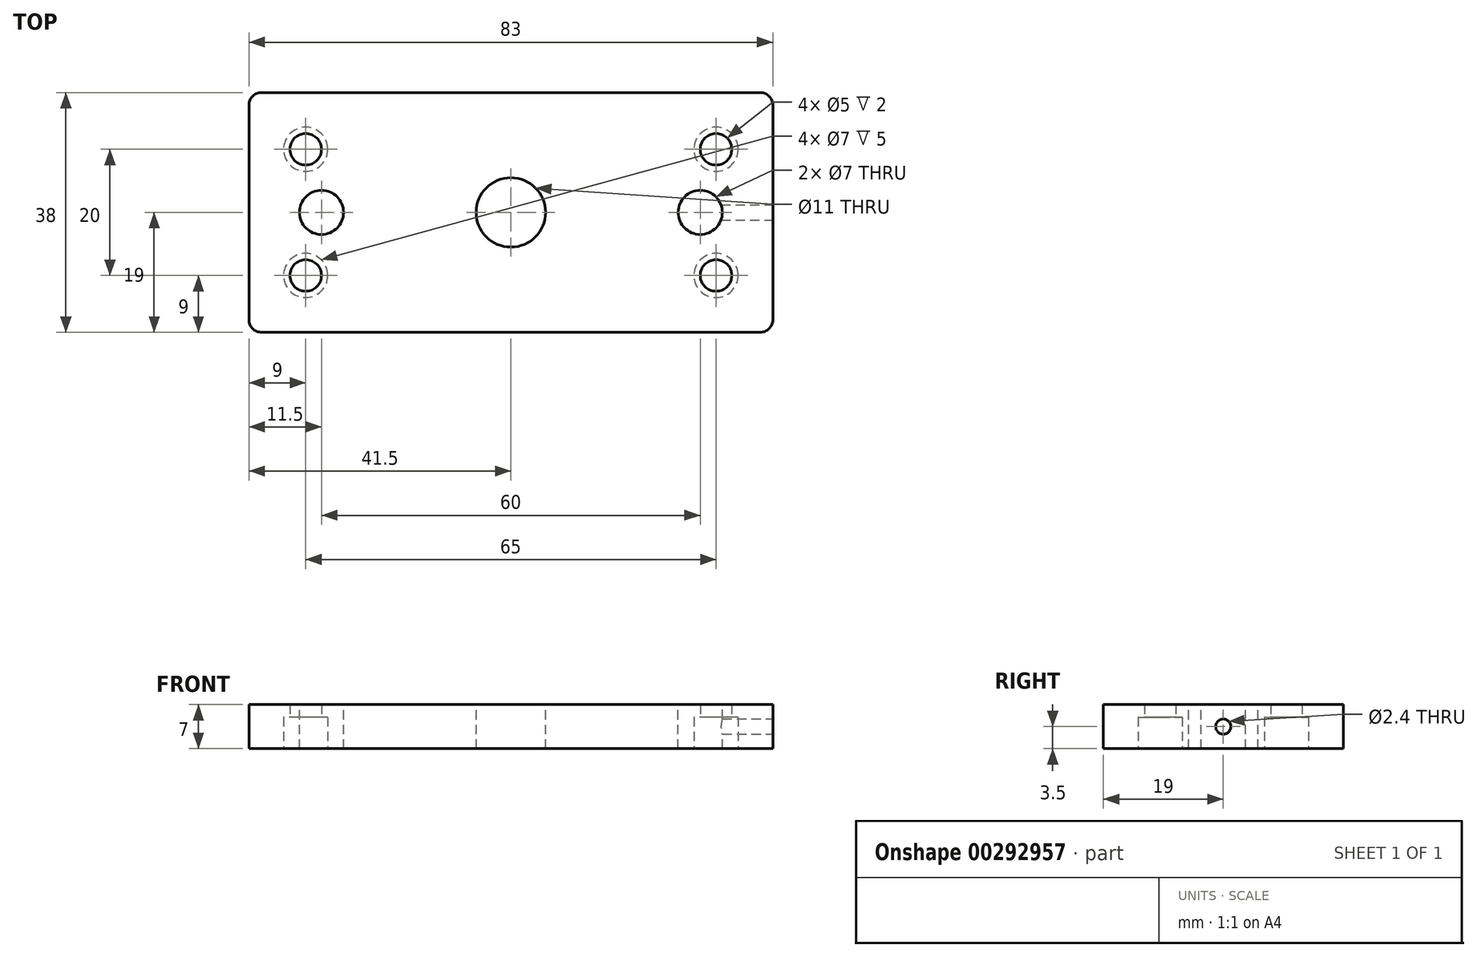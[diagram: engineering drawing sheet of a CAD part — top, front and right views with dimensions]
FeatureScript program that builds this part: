
annotation { "Feature Type Name" : "Feature", "Feature Type Description" : "" }
export const myFeature = defineFeature(function(context is Context, id is Id, definition is map)
    precondition{}
    {
        {
            var Q0;
            Q0=qCreatedBy(makeId("Top.planeOp"),FACE);
            var sketch = newSketch(context, id + "F0", { "sketchPlane" : qUnion([Q0])});
            skLineSegment(sketch, "E0.bottom", {"start": v(0, 0) * mm, "end": v(-65, 0) * mm});
            skLineSegment(sketch, "E0.top", {"start": v(0, 20) * mm, "end": v(-65, 20) * mm});
            skLineSegment(sketch, "E0.left", {"start": v(0, 0) * mm, "end": v(0, 20) * mm});
            skLineSegment(sketch, "E0.right", {"start": v(-65, 0) * mm, "end": v(-65, 20) * mm});
            skLineSegment(sketch, "E1.0", {"start": v(7, 29) * mm, "end": v(-72, 29) * mm});
            skLineSegment(sketch, "E1.1", {"start": v(9, -7) * mm, "end": v(9, 27) * mm});
            skLineSegment(sketch, "E1.2", {"start": v(7, -9) * mm, "end": v(-72, -9) * mm});
            skLineSegment(sketch, "E1.3", {"start": v(-74, -7) * mm, "end": v(-74, 27) * mm});
            skPoint(sketch, "E2.visualSharp", {"position": v(-74, 29) * mm});
            skArc(sketch, "E2.filletArc", {"start": v(-72, 29) * mm, "mid": v(-73.41, 28.41) * mm, "end": v(-74, 27) * mm});
            skPoint(sketch, "E3.visualSharp", {"position": v(-74, -9) * mm});
            skArc(sketch, "E3.filletArc", {"start": v(-74, -7) * mm, "mid": v(-73.41, -8.41) * mm, "end": v(-72, -9) * mm});
            skPoint(sketch, "E4.visualSharp", {"position": v(9, -9) * mm});
            skArc(sketch, "E4.filletArc", {"start": v(7, -9) * mm, "mid": v(8.41, -8.41) * mm, "end": v(9, -7) * mm});
            skPoint(sketch, "E5.visualSharp", {"position": v(9, 29) * mm});
            skArc(sketch, "E5.filletArc", {"start": v(9, 27) * mm, "mid": v(8.41, 28.41) * mm, "end": v(7, 29) * mm});
            skSolve(sketch);
        }
        {
            var Q0;
            Q0=makeQuery(id+"F0.imprint","IMPRINT",FACE,{"disambiguationData":[TD([[makeQuery(id+"F0.imprint","IMPRINT",EDGE,{"derivedFrom":sQuery(id+"F0.wireOp",EDGE,"E0.bottom")}),1.0]])]});
            var Q1;
            Q1=makeQuery(id+"F0.imprint","IMPRINT",FACE,{"disambiguationData":[TD([[makeQuery(id+"F0.imprint","IMPRINT",EDGE,{"derivedFrom":sQuery(id+"F0.wireOp",EDGE,"E0.bottom")}),-1.0]])]});
            extrude(context, id + "F1", {"entities" : qUnion([Q0, Q1]), "depth" : 7 * mm});
        }
        {
            var Q0;
            Q0=sQuery(id+"F0.wireOp",VERTEX,"E0.right.end");
            var Q1;
            Q1=sQuery(id+"F0.wireOp",VERTEX,"E0.right.start");
            var Q2;
            Q2=sQuery(id+"F0.wireOp",VERTEX,"E0.left.start");
            var Q3;
            Q3=sQuery(id+"F0.wireOp",VERTEX,"E0.left.end");
            var Q4;
            Q4=makeQuery(id+"F1.opExtrude","SWEPT_BODY",BODY,{"disambiguationData":[OSD([sQuery(id+"F0.wireOp",EDGE,"E1.0"),sQuery(id+"F0.wireOp",EDGE,"E1.1"),sQuery(id+"F0.wireOp",EDGE,"E1.2"),sQuery(id+"F0.wireOp",EDGE,"E1.3"),sQuery(id+"F0.wireOp",EDGE,"E2.filletArc"),sQuery(id+"F0.wireOp",EDGE,"E3.filletArc"),sQuery(id+"F0.wireOp",EDGE,"E4.filletArc"),sQuery(id+"F0.wireOp",EDGE,"E5.filletArc")])]});
            hole(context, id + "F2", {"style" : HoleStyle.SIMPLE, "endStyle" : HoleEndStyle.THROUGH, "oppositeDirection" : true, "holeDiameter" : 5 * mm, "tappedDepth" : 12 * mm, "tapClearance" : 3, "locations" : qUnion([Q0, Q1, Q2, Q3]), "scope" : qUnion([Q4])});
        }
        {
            var Q0;
            Q0=makeQuery(id+"F1.opExtrude","CAP_FACE",FACE,{"disambiguationData":[OSD([sQuery(id+"F0.wireOp",EDGE,"E1.0"),sQuery(id+"F0.wireOp",EDGE,"E1.1"),sQuery(id+"F0.wireOp",EDGE,"E1.2"),sQuery(id+"F0.wireOp",EDGE,"E1.3"),sQuery(id+"F0.wireOp",EDGE,"E2.filletArc"),sQuery(id+"F0.wireOp",EDGE,"E3.filletArc"),sQuery(id+"F0.wireOp",EDGE,"E4.filletArc"),sQuery(id+"F0.wireOp",EDGE,"E5.filletArc")])],"isStart":false});
            var sketch = newSketch(context, id + "F3", { "sketchPlane" : qUnion([Q0])});
            skCircle(sketch, "E6", {"center": v(-62.5, 10) * mm, "radius": 3.5 * mm});
            skCircle(sketch, "E7", {"center": v(-2.5, 10) * mm, "radius": 3.5 * mm});
            skSolve(sketch);
        }
        {
            var Q0;
            Q0=makeQuery(id+"F3.imprint","IMPRINT",FACE,{"disambiguationData":[TD([[makeQuery(id+"F3.imprint","IMPRINT",EDGE,{"derivedFrom":sQuery(id+"F3.wireOp",EDGE,"E6")}),1.0]])]});
            var Q1;
            Q1=makeQuery(id+"F3.imprint","IMPRINT",FACE,{"disambiguationData":[TD([[makeQuery(id+"F3.imprint","IMPRINT",EDGE,{"derivedFrom":sQuery(id+"F3.wireOp",EDGE,"E7")}),1.0]])]});
            extrude(context, id + "F4", {"entities" : qUnion([Q0, Q1]), "operationType" : NewBodyOperationType.REMOVE, "oppositeDirection" : true, "depth" : 25 * mm});
        }
        {
            var Q0;
            Q0=makeQuery(id+"F1.opExtrude","SWEPT_FACE",FACE,{"disambiguationData":[OSD([sQuery(id+"F0.wireOp",EDGE,"E1.1")])]});
            var sketch = newSketch(context, id + "F5", { "sketchPlane" : qUnion([Q0])});
            skCircle(sketch, "E8", {"center": v(10, 3.5) * mm, "radius": 1.5 * mm});
            skSolve(sketch);
        }
        {
            var Q0;
            Q0=sQuery(id+"F5.wireOp",VERTEX,"E8.center");
            var Q1;
            Q1=makeQuery(id+"F1.opExtrude","SWEPT_BODY",BODY,{"disambiguationData":[OSD([sQuery(id+"F0.wireOp",EDGE,"E1.0"),sQuery(id+"F0.wireOp",EDGE,"E1.1"),sQuery(id+"F0.wireOp",EDGE,"E1.2"),sQuery(id+"F0.wireOp",EDGE,"E1.3"),sQuery(id+"F0.wireOp",EDGE,"E2.filletArc"),sQuery(id+"F0.wireOp",EDGE,"E3.filletArc"),sQuery(id+"F0.wireOp",EDGE,"E4.filletArc"),sQuery(id+"F0.wireOp",EDGE,"E5.filletArc")])]});
            hole(context, id + "F6", {"style" : HoleStyle.SIMPLE, "endStyle" : HoleEndStyle.BLIND, "standardTappedOrClearance" : lookupTablePath({ "standard" : "ISO", "engagement" : "75%", "pitch" : "0.6 mm", "size" : "M3", "type" : "Tapped" }), "standardBlindInLast" : lookupTablePath({ "standard" : "ISO", "engagement" : "75%", "pitch" : "0.6 mm", "size" : "M3", "type" : "Tapped" }), "holeDiameter" : 2.4 * mm, "showTappedDepth" : true, "holeDepth" : 11.8 * mm, "tappedDepth" : 10 * mm, "tapClearance" : 3, "locations" : qUnion([Q0]), "scope" : qUnion([Q1])});
        }
        {
            var Q0;
            Q0=makeQuery(id+"F1.opExtrude","SWEPT_FACE",FACE,{"disambiguationData":[OSD([sQuery(id+"F0.wireOp",EDGE,"E1.1")])]});
            cPlane(context, id + "F7", {"entities" : qUnion([Q0]), "cplaneType" : CPlaneType.OFFSET, "offset" : 41.5 * mm, "oppositeDirection" : true, "width" : 150 * mm, "height" : 150 * mm});
        }
        {
            var Q0;
            Q0=makeQuery(id+"F1.opExtrude","CAP_FACE",FACE,{"disambiguationData":[OSD([sQuery(id+"F0.wireOp",EDGE,"E1.0"),sQuery(id+"F0.wireOp",EDGE,"E1.1"),sQuery(id+"F0.wireOp",EDGE,"E1.2"),sQuery(id+"F0.wireOp",EDGE,"E1.3"),sQuery(id+"F0.wireOp",EDGE,"E2.filletArc"),sQuery(id+"F0.wireOp",EDGE,"E3.filletArc"),sQuery(id+"F0.wireOp",EDGE,"E4.filletArc"),sQuery(id+"F0.wireOp",EDGE,"E5.filletArc")])],"isStart":false});
            var sketch = newSketch(context, id + "F8", { "sketchPlane" : qUnion([Q0])});
            skCircle(sketch, "E9", {"center": v(-32.5, 10) * mm, "radius": 5.5 * mm});
            skSolve(sketch);
        }
        {
            var Q0;
            Q0=makeQuery(id+"F8.imprint","IMPRINT",FACE,{"disambiguationData":[TD([[makeQuery(id+"F8.imprint","IMPRINT",EDGE,{"derivedFrom":sQuery(id+"F8.wireOp",EDGE,"E9")}),1.0]])]});
            extrude(context, id + "F9", {"entities" : qUnion([Q0]), "operationType" : NewBodyOperationType.REMOVE, "oppositeDirection" : true, "depth" : 25 * mm});
        }
        {
            var Q0;
            Q0=makeQuery(id+"F0.imprint","IMPRINT",FACE,{"disambiguationData":[TD([[makeQuery(id+"F0.imprint","IMPRINT",EDGE,{"derivedFrom":sQuery(id+"F0.wireOp",EDGE,"E0.bottom")}),1.0]])]});
            var sketch = newSketch(context, id + "F10", { "sketchPlane" : qUnion([Q0])});
            skCircle(sketch, "E10", {"center": v(0, 0) * mm, "radius": 3.5 * mm});
            skCircle(sketch, "E11", {"center": v(-65, 0) * mm, "radius": 3.5 * mm});
            skCircle(sketch, "E12", {"center": v(0, 20) * mm, "radius": 3.5 * mm});
            skCircle(sketch, "E13", {"center": v(-65, 20) * mm, "radius": 3.5 * mm});
            skSolve(sketch);
        }
        {
            var Q0;
            Q0 = qSketchRegion(id + "F10", true);
            extrude(context, id + "F11", {"entities" : qUnion([Q0]), "operationType" : NewBodyOperationType.REMOVE, "depth" : 5 * mm});
        }
    });
